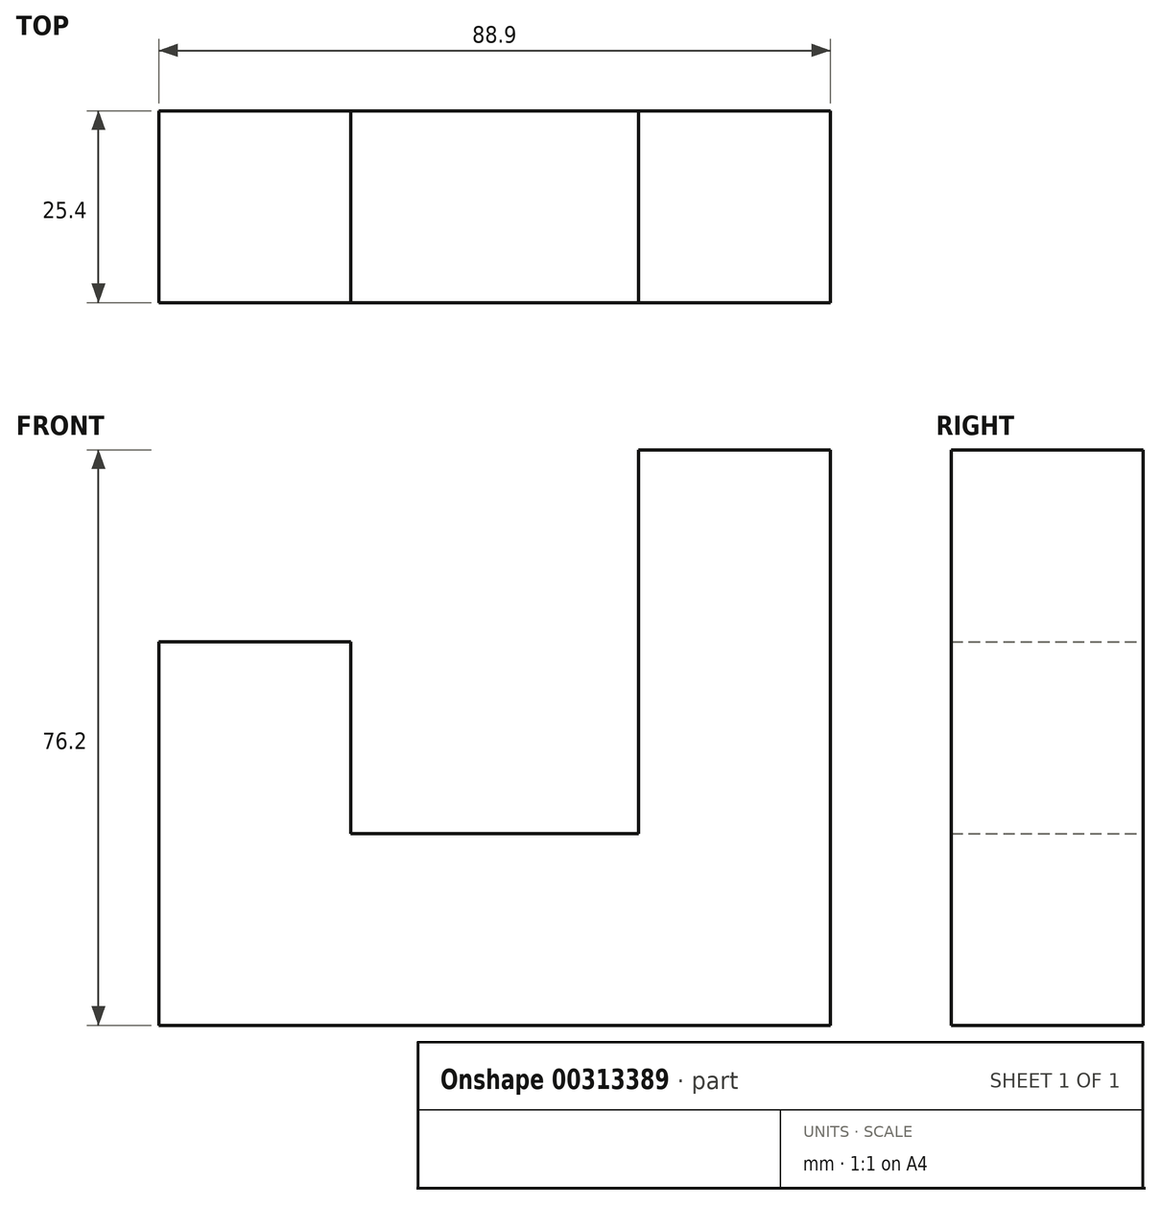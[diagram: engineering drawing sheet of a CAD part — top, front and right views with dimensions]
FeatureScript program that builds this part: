
annotation { "Feature Type Name" : "Feature", "Feature Type Description" : "" }
export const myFeature = defineFeature(function(context is Context, id is Id, definition is map)
    precondition{}
    {
        {
            var Q0;
            Q0=qCreatedBy(makeId("Front.planeOp"),FACE);
            var sketch = newSketch(context, id + "F0", { "sketchPlane" : qUnion([Q0])});
            skLineSegment(sketch, "E0", {"start": v(-42.28, -46.27) * mm, "end": v(46.62, -46.27) * mm});
            skLineSegment(sketch, "E1", {"start": v(46.62, -46.27) * mm, "end": v(46.62, 29.93) * mm});
            skLineSegment(sketch, "E2", {"start": v(46.62, 29.93) * mm, "end": v(21.22, 29.93) * mm});
            skLineSegment(sketch, "E3", {"start": v(21.22, 29.93) * mm, "end": v(21.22, -20.87) * mm});
            skLineSegment(sketch, "E4", {"start": v(21.22, -20.87) * mm, "end": v(-16.88, -20.87) * mm});
            skLineSegment(sketch, "E5", {"start": v(-16.88, -20.87) * mm, "end": v(-16.88, 4.53) * mm});
            skLineSegment(sketch, "E6", {"start": v(-16.88, 4.53) * mm, "end": v(-42.28, 4.53) * mm});
            skLineSegment(sketch, "E7", {"start": v(-42.28, 4.53) * mm, "end": v(-42.28, -46.27) * mm});
            skSolve(sketch);
        }
        {
            var Q0;
            Q0=makeQuery(id+"F0.imprint","IMPRINT",FACE,{"disambiguationData":[TD([[makeQuery(id+"F0.imprint","IMPRINT",EDGE,{"derivedFrom":sQuery(id+"F0.wireOp",EDGE,"E0")}),1.0]])]});
            extrude(context, id + "F1", {"entities" : qUnion([Q0]), "depth" : 25.4 * mm});
        }
    });
